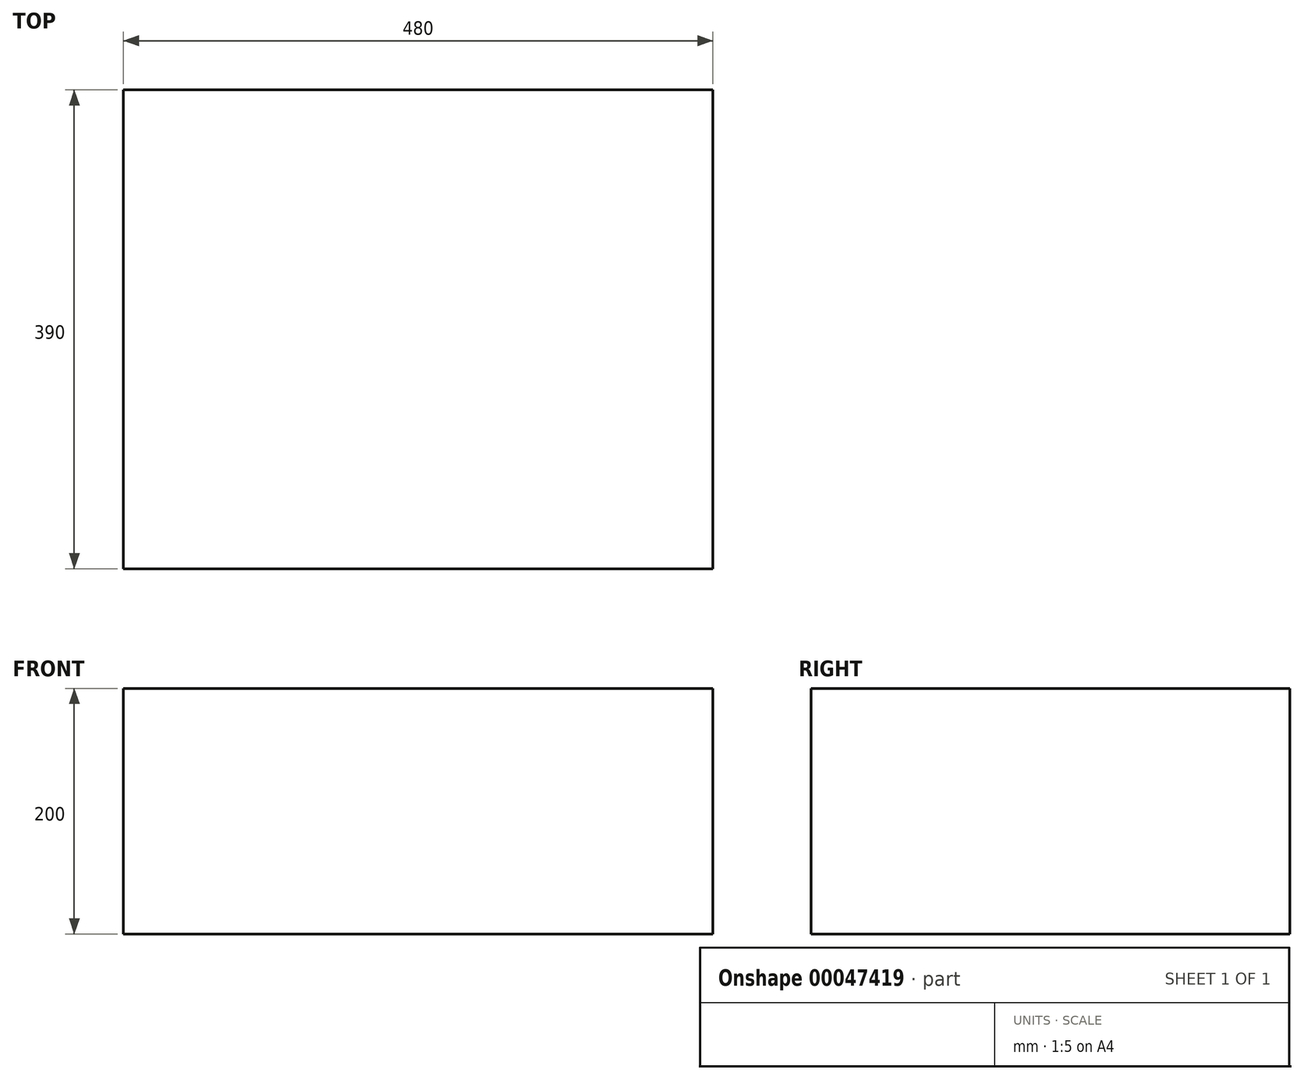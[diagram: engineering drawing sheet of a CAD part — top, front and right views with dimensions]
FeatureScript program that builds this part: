
annotation { "Feature Type Name" : "Feature", "Feature Type Description" : "" }
export const myFeature = defineFeature(function(context is Context, id is Id, definition is map)
    precondition{}
    {
        {
            var Q0;
            Q0=qCreatedBy(makeId("Top.planeOp"),FACE);
            var sketch = newSketch(context, id + "F0", { "sketchPlane" : qUnion([Q0])});
            skLineSegment(sketch, "E0.rect.bottom", {"start": v(240, 195) * mm, "end": v(-240, 195) * mm});
            skLineSegment(sketch, "E0.rect.top", {"start": v(240, -195) * mm, "end": v(-240, -195) * mm});
            skLineSegment(sketch, "E0.rect.left", {"start": v(240, 195) * mm, "end": v(240, -195) * mm});
            skLineSegment(sketch, "E0.rect.right", {"start": v(-240, 195) * mm, "end": v(-240, -195) * mm});
            skPoint(sketch, "E0.rect.middle", {"position": v(0, 0) * mm});
            skSolve(sketch);
        }
        {
            var Q0;
            Q0 = qSketchRegion(id + "F0", true);
            extrude(context, id + "F1", {"entities" : qUnion([Q0]), "depth" : 200 * mm});
        }
    });
